# Revit family: Hängebügel Typ L
name_source: partatom
category: HLS-Bauteile
revit_build: Autodesk Revit 2017 (Build: 20190507_1515(x64)
units: mm (PartAtom-declared; Revit-internal decimal feet)

## family parameters
Arbeitsebenenbasiert = Ja
Beim Laden mit Abzugskörper schneiden = Nein
Bemaßung runder Anschluss = Durchmesser verwenden
Gemeinsam genutzt = Ja
Immer vertikal = Nein
Raumberechnungspunkt = Nein
Teiletyp = Normal

## types (2) — shared parameters
Breite = 29 mm  [stored 0.0951444 ft]
Fabrikat = MEFA
Firma = MEFA Befestigungs- und Montagesysteme GmbH
Kurztext1 = Hängebügel Typ L verst. H 30 mm
Länge = 35 mm  [stored 0.114829 ft]
Mengeneinheit = St
Vorgabe-Ansicht = 1219 mm
vpe = 100 St

## per-type parameters (varying)
| type | A | Artikelnummer | EAN | Gewicht | Gewicht pro Bauteil | Konusmutter | Kurztext2 | Sechskantmutter |
| Hängebügel Typ L M 8 | 12 mm  [stored 0.0393701 ft] | 0781010 | 4250928418692 | 0.10 kg | 0.10 kg | Konusmutter M 8 | für Gewinde M8 | Sechskantmutter : Sechskantmutter M8 |
| Hängebügel Typ L M10 | 14 mm  [stored 0.0459318 ft] | 0781029 | 4250928418708 | 0.12 kg | 0.12 kg | Konusmutter M10 | für Gewinde M10 | Sechskantmutter : Sechskantmutter M10 |

note: [stored X ft] marks values corroborated as IEEE doubles in the binary element streams (Revit-internal decimal feet)

## geometry (parser evidence)
native form markers: Sweep x4
no freeform markers — native parametric forms only
